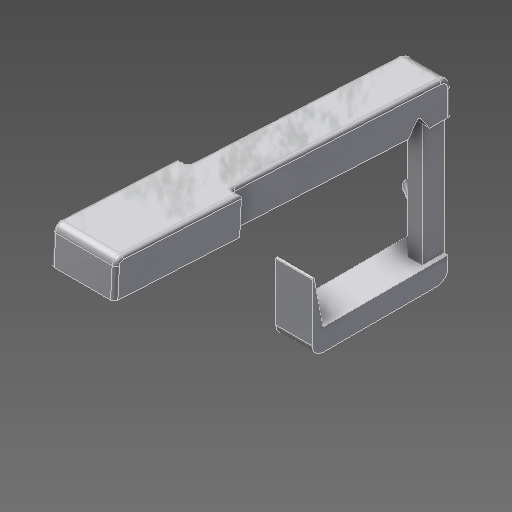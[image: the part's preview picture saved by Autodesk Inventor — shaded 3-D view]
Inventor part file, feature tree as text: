
AUTODESK INVENTOR PART (.ipt)
format: ipt  version: 2020 (Build 240168000, 168)  size: 325,632 bytes
history: native  units: mm
features: extrude x7, fillet x6, other x3, draft x1, chamfer x1
ambient origin geometry x8: Origin, YZ Plane, XZ Plane, XY Plane, X Axis, Y Axis, Z Axis, Center Point
bodies: Solid1 (feature_tree)
feature tree (18):
  other  "Key Sketch"
  extrude  "Upper Key"  Depth=10.0mm
  extrude  "Lower Key"  Depth=1.0mm
  other  "Hinge Cut Sketch"
  extrude  "Hinge Cut"  Depth=10.0mm TaperAngle=0.0deg
  extrude  "Hinge Cut 2"  Depth=3.0mm
  other  "Lever Sketch"
  extrude  "Vertical Lever"  Depth=3.0mm
  extrude  "Horizontal Lever"  Depth=33.6625mm
  extrude  "Spring Hook"  Depth=0.5mm
  draft  "FaceDraft3"
  chamfer  "Chamfer1"  Distance=3.0mm
  fillet  "Fillet9"  Radius=6.0mm
  fillet  "Fillet10"  Radius=4.0mm
  fillet  "Fillet5"  Radius=10.0mm
  fillet  "Fillet4"  [1 undecoded]
  fillet  "Fillet11"  Radius=3.0mm
  fillet  "Fillet14"  Radius=2.3mm
note: 1 required parameter value undecoded (feature->parameter linkage not recoverable at this tier; creation-order binding heuristic only, values carry confidence <= 0.55)
